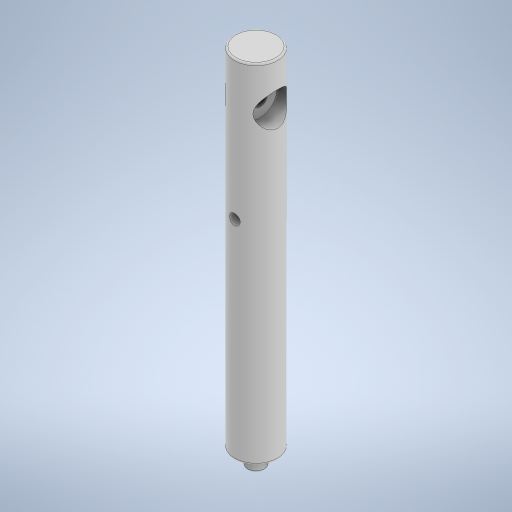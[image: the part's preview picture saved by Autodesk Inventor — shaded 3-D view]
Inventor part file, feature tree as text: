
AUTODESK INVENTOR PART (.ipt)
format: ipt  version: 2023.2 (Build 272271030, 271C)  size: 655,872 bytes
history: native  units: mm
features: extrude x11, sketch x10, projected_geometry x5, fillet x1
ambient origin geometry x8: Origin, YZ Plane, XZ Plane, XY Plane, X Axis, Y Axis, Z Axis, Center Point
bodies: Solid1 (feature_tree)
feature tree (27):
  extrude  "Extrusion1"  Depth=200.0mm TaperAngle=0.0deg
  sketch  "Sketch6"  dims[d7=25.0mm d8=19.3mm]
  extrude  "Extrusion3"  Depth=19.3mm
  extrude  "Extrusion4"  Depth=10.0mm TaperAngle=0.0deg
  extrude  "Extrusion5"  Depth=15.0mm TaperAngle=0.0deg
  extrude  "Extrusion6"  Depth=9.0mm TaperAngle=0.0deg
  extrude  "Extrusion7"  Depth=10.0mm TaperAngle=0.0deg
  extrude  "Extrusion8"  Depth=24.5mm TaperAngle=0.0deg
  extrude  "Extrusion9"  Depth=1.0mm TaperAngle=0.0deg
  fillet  "Fillet4"  Radius=1.0mm
  extrude  "Extrusion10"  Depth=150.0mm TaperAngle=0.0deg
  extrude  "Extrusion11"  Depth=10.0mm
  extrude  "Extrusion12"  Depth=10.0mm
  sketch  "Sketch1"  dims[d0=24.85mm d1=200.0mm d2=0.0mm]
  sketch  "Sketch8"  dims[d9=12.45mm d10=50.0mm d11=0.0mm d12=0.0mm d14=10.0mm d15=0.0mm]
  projected_geometry  "Projected Loop1"
  sketch  "Sketch9"  dims[d16=7.8mm d17=15.0mm d18=0.0mm]
  sketch  "Sketch10"  dims[d19=9.9mm d20=9.0mm d21=0.0mm]
  sketch  "Sketch11"  dims[d22=5.2mm d23=10.0mm d24=0.0mm]
  sketch  "Sketch12"  dims[d25=80.0mm d26=24.5mm d27=0.0mm]
  projected_geometry  "Projected Loop2"
  sketch  "Sketch13"  dims[d28=6.1mm d29=50.0mm d30=0.0mm d33=1.0mm]
  projected_geometry  "Projected Loop3"
  sketch  "Sketch15"  dims[d39=12.45mm d40=0.0mm d41=150.0mm d42=0.0mm]
  projected_geometry  "Projected Loop4"
  sketch  "Sketch16"  dims[d43=10.0mm d44=0.0mm d35=0.5mm d36=0.872665mm d37=0.5mm d38=0.872665mm d45=0.5mm d46=0.872665mm]
  projected_geometry  "Projected Loop5"
